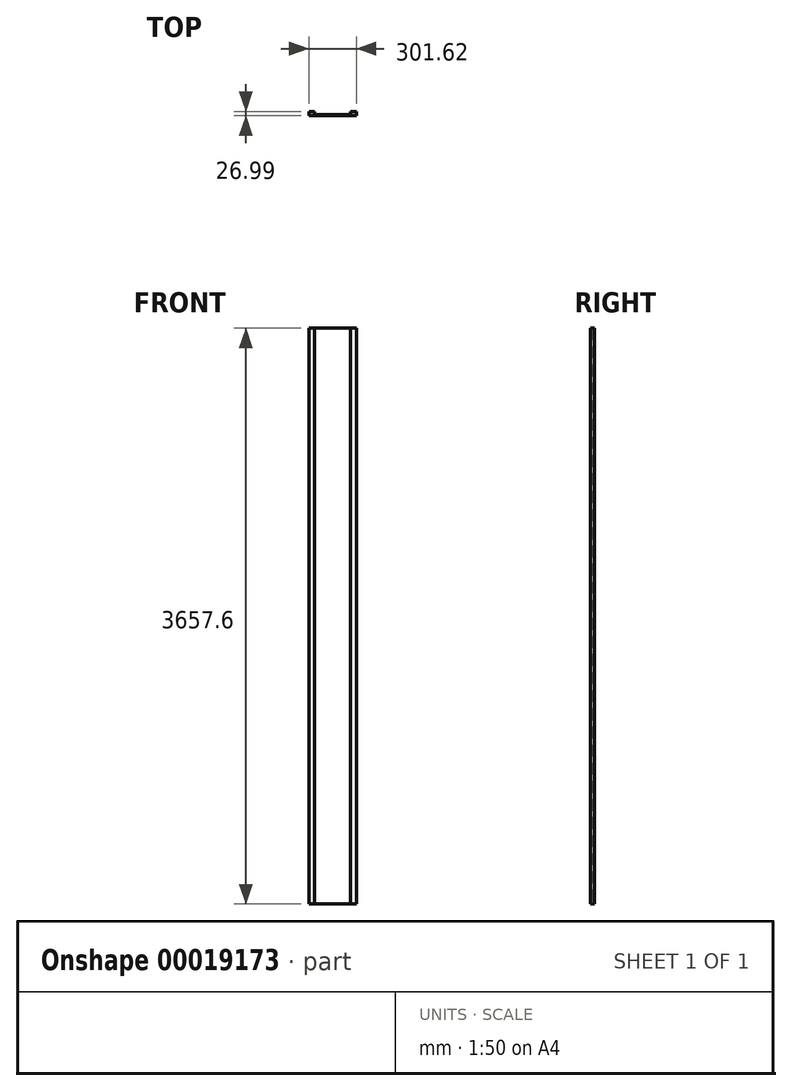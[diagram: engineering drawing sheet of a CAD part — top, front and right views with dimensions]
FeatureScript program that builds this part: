
annotation { "Feature Type Name" : "Feature", "Feature Type Description" : "" }
export const myFeature = defineFeature(function(context is Context, id is Id, definition is map)
    precondition{}
    {
        {
            var Q0;
            Q0=qCreatedBy(makeId("Top.planeOp"),FACE);
            var sketch = newSketch(context, id + "F0", { "sketchPlane" : qUnion([Q0])});
            skLineSegment(sketch, "E0.rect.bottom", {"start": v(115.89, 3.18) * mm, "end": v(-115.89, 3.18) * mm});
            skLineSegment(sketch, "E0.rect.top", {"start": v(115.89, -3.17) * mm, "end": v(-115.89, -3.17) * mm});
            skPoint(sketch, "E0.rect.middle", {"position": v(0, 0) * mm});
            skLineSegment(sketch, "E1.top", {"start": v(-150.81, 22.22) * mm, "end": v(-115.89, 22.22) * mm});
            skLineSegment(sketch, "E1.right", {"start": v(-115.89, 3.17) * mm, "end": v(-115.89, 22.22) * mm});
            skLineSegment(sketch, "E2.right", {"start": v(-115.89, -22.22) * mm, "end": v(-115.89, -3.17) * mm});
            skLineSegment(sketch, "E2.bottom", {"start": v(-150.81, -22.22) * mm, "end": v(-115.89, -22.22) * mm});
            skLineSegment(sketch, "E3", {"start": v(-150.81, 22.22) * mm, "end": v(-150.81, -22.22) * mm});
            skLineSegment(sketch, "E4.MirrorCS", {"start": v(150.81, -22.22) * mm, "end": v(115.89, -22.22) * mm});
            skLineSegment(sketch, "E5.MirrorCS", {"start": v(115.89, 3.17) * mm, "end": v(115.89, 22.22) * mm});
            skLineSegment(sketch, "E6.MirrorCS", {"start": v(115.89, -22.22) * mm, "end": v(115.89, -3.17) * mm});
            skLineSegment(sketch, "E7.MirrorCS", {"start": v(150.81, 22.22) * mm, "end": v(115.89, 22.22) * mm});
            skLineSegment(sketch, "E8", {"start": v(150.81, 22.22) * mm, "end": v(150.81, -22.22) * mm});
            skSolve(sketch);
        }
        {
            var Q0;
            Q0 = qSketchRegion(id + "F0", true);
            extrude(context, id + "F1", {"entities" : qUnion([Q0]), "depth" : 3657.6 * mm});
        }
        {
            var Q0;
            Q0=makeQuery(id+"F1.opExtrude","SWEPT_FACE",FACE,{"disambiguationData":[OSD([sQuery(id+"F0.wireOp",EDGE,"E8")])]});
            var sketch = newSketch(context, id + "F2", { "sketchPlane" : qUnion([Q0])});
            skLineSegment(sketch, "E9.bottom", {"start": v(-22.22, 3657.6) * mm, "end": v(-4.76, 3657.6) * mm});
            skLineSegment(sketch, "E9.top", {"start": v(-22.22, 0) * mm, "end": v(-4.76, 0) * mm});
            skLineSegment(sketch, "E9.left", {"start": v(-22.22, 3657.6) * mm, "end": v(-22.22, 0) * mm});
            skLineSegment(sketch, "E9.right", {"start": v(-4.76, 3657.6) * mm, "end": v(-4.76, 0) * mm});
            skLineSegment(sketch, "E10", {"start": v(0, 3657.6) * mm, "end": v(0, 0) * mm, "construction": true});
            skSolve(sketch);
        }
        {
            var Q0;
            Q0 = qSketchRegion(id + "F2", true);
            extrude(context, id + "F3", {"entities" : qUnion([Q0]), "operationType" : NewBodyOperationType.REMOVE, "endBound" : BoundingType.THROUGH_ALL, "oppositeDirection" : true, "depth" : 25.4 * mm});
        }
    });
